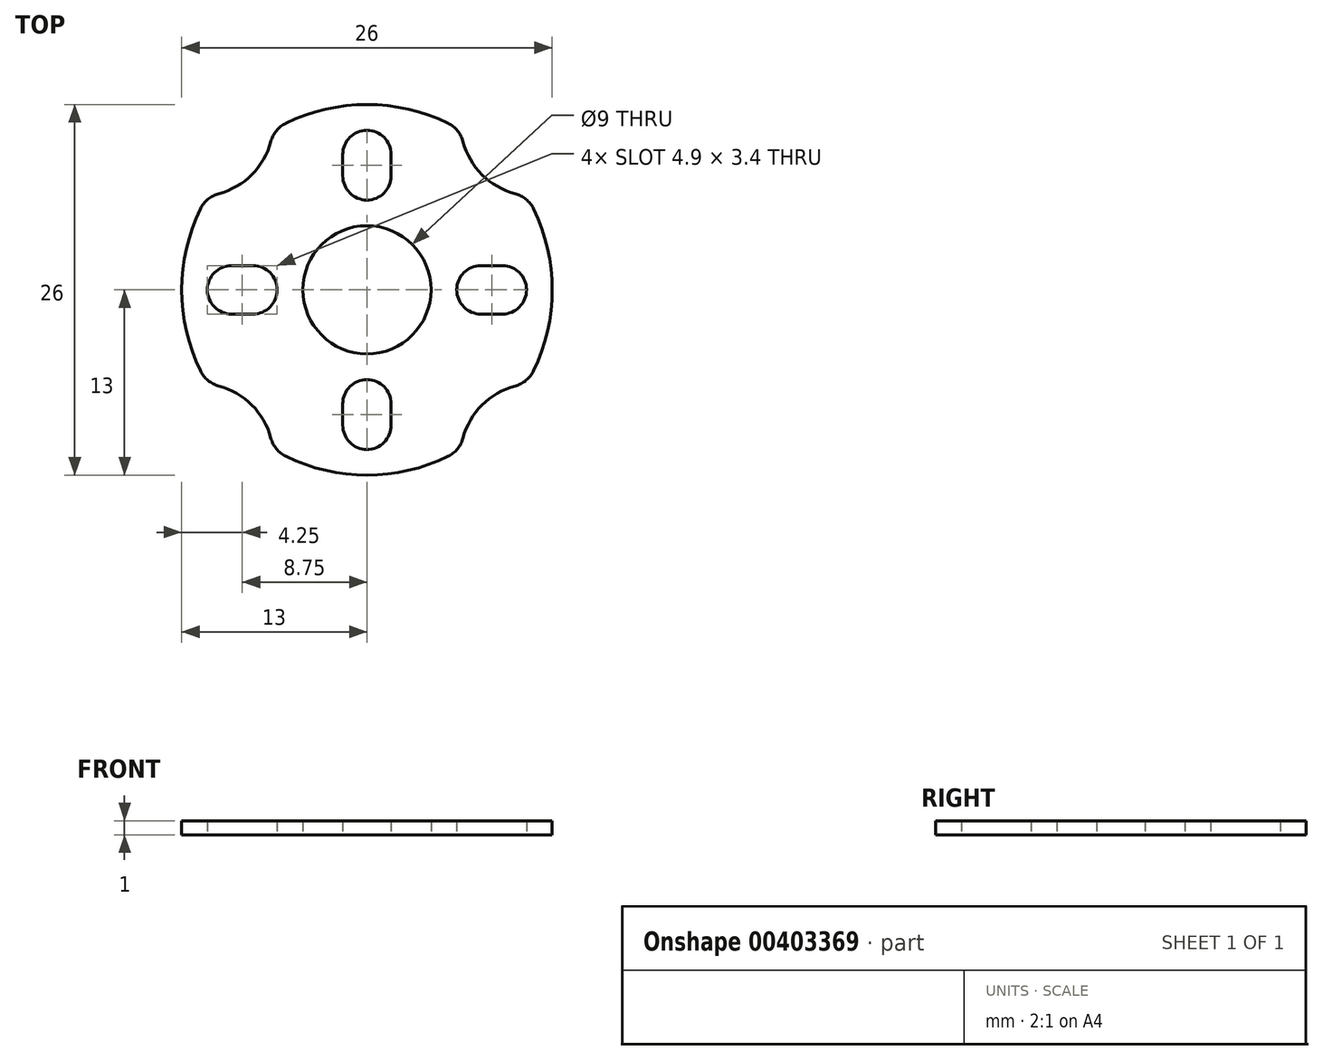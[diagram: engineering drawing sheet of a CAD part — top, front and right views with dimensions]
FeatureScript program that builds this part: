
annotation { "Feature Type Name" : "Feature", "Feature Type Description" : "" }
export const myFeature = defineFeature(function(context is Context, id is Id, definition is map)
    precondition{}
    {
        {
            assignVariable(context, id + "F0", {"name" : "padThickness", "anyValue" : 1});
        }
        {
            var Q0;
            Q0=qCreatedBy(makeId("Top.planeOp"),FACE);
            var sketch = newSketch(context, id + "F1", { "sketchPlane" : qUnion([Q0])});
            skLineSegment(sketch, "E0", {"start": v(-16.5, -1.7) * mm, "end": v(-16.5, -1.7) * mm});
            skLineSegment(sketch, "E1", {"start": v(-16.5, 1.7) * mm, "end": v(-8, 1.7) * mm});
            skLineSegment(sketch, "E2", {"start": v(1.7, 16.5) * mm, "end": v(1.7, 8) * mm});
            skLineSegment(sketch, "E3", {"start": v(-1.7, 16.5) * mm, "end": v(-1.7, 8) * mm});
            skLineSegment(sketch, "E4.MirrorCS", {"start": v(-1.7, -16.5) * mm, "end": v(-1.7, -16.5) * mm});
            skLineSegment(sketch, "E5.MirrorCS", {"start": v(1.7, -16.5) * mm, "end": v(1.7, -8) * mm});
            skLineSegment(sketch, "E6.MirrorCS", {"start": v(16.5, 1.7) * mm, "end": v(8, 1.7) * mm});
            skLineSegment(sketch, "E7.MirrorCS", {"start": v(16.5, -1.7) * mm, "end": v(8, -1.7) * mm});
            skArc(sketch, "E8", {"start": v(-1.7, 16.5) * mm, "mid": v(0, 14.8) * mm, "end": v(1.7, 16.5) * mm});
            skArc(sketch, "E9", {"start": v(1.7, 16.5) * mm, "mid": v(0, 18.2) * mm, "end": v(-1.7, 16.5) * mm});
            skLineSegment(sketch, "E10", {"start": v(-1.7, 8) * mm, "end": v(-1.7, 8) * mm});
            skLineSegment(sketch, "E11", {"start": v(8, 1.7) * mm, "end": v(8, 1.7) * mm});
            skArc(sketch, "E12", {"start": v(8, -1.7) * mm, "mid": v(6.3, 0) * mm, "end": v(8, 1.7) * mm});
            skArc(sketch, "E13", {"start": v(8, 1.7) * mm, "mid": v(9.7, 0) * mm, "end": v(8, -1.7) * mm});
            skArc(sketch, "E14", {"start": v(16.5, 1.7) * mm, "mid": v(18.2, 0) * mm, "end": v(16.5, -1.7) * mm});
            skArc(sketch, "E15", {"start": v(16.5, -1.7) * mm, "mid": v(14.8, 0) * mm, "end": v(16.5, 1.7) * mm});
            skLineSegment(sketch, "E16", {"start": v(1.7, -8) * mm, "end": v(1.7, -8) * mm});
            skArc(sketch, "E17", {"start": v(-1.7, -8) * mm, "mid": v(0, -6.3) * mm, "end": v(1.7, -8) * mm});
            skArc(sketch, "E18", {"start": v(1.7, -8) * mm, "mid": v(0, -9.7) * mm, "end": v(-1.7, -8) * mm});
            skLineSegment(sketch, "E19", {"start": v(-1.7, -16.5) * mm, "end": v(-1.7, -8) * mm});
            skArc(sketch, "E20", {"start": v(1.7, -16.5) * mm, "mid": v(0, -18.2) * mm, "end": v(-1.7, -16.5) * mm});
            skArc(sketch, "E21", {"start": v(-1.7, -16.5) * mm, "mid": v(0, -14.8) * mm, "end": v(1.7, -16.5) * mm});
            skLineSegment(sketch, "E22", {"start": v(-16.5, -1.7) * mm, "end": v(-8, -1.7) * mm});
            skArc(sketch, "E23", {"start": v(-16.5, -1.7) * mm, "mid": v(-14.8, 0) * mm, "end": v(-16.5, 1.7) * mm});
            skArc(sketch, "E24", {"start": v(-16.5, 1.7) * mm, "mid": v(-18.2, 0) * mm, "end": v(-16.5, -1.7) * mm});
            skArc(sketch, "E25", {"start": v(-8, 1.7) * mm, "mid": v(-9.7, 0) * mm, "end": v(-8, -1.7) * mm});
            skArc(sketch, "E26", {"start": v(-8, -1.7) * mm, "mid": v(-6.3, 0) * mm, "end": v(-8, 1.7) * mm});
            skArc(sketch, "E27", {"start": v(1.7, 8) * mm, "mid": v(0, 9.7) * mm, "end": v(-1.7, 8) * mm});
            skArc(sketch, "E28", {"start": v(-1.7, 8) * mm, "mid": v(0, 6.3) * mm, "end": v(1.7, 8) * mm});
            skArc(sketch, "E29.0", {"start": v(-16.5, 3.14) * mm, "mid": v(-18.72, 2.22) * mm, "end": v(-19.64, 0) * mm});
            skArc(sketch, "E30.0", {"start": v(0, 19.64) * mm, "mid": v(-2.22, 18.72) * mm, "end": v(-3.14, 16.5) * mm});
            skArc(sketch, "E31", {"start": v(-8, 3.14) * mm, "mid": v(-4.6, 4.6) * mm, "end": v(-3.14, 8) * mm});
            skLineSegment(sketch, "E32", {"start": v(-8, 3.14) * mm, "end": v(-16.5, 3.14) * mm});
            skLineSegment(sketch, "E33", {"start": v(-3.14, 8) * mm, "end": v(-3.14, 16.5) * mm});
            skPoint(sketch, "E34", {"position": v(-19.64, 0) * mm});
            skPoint(sketch, "E35", {"position": v(0, 19.64) * mm});
            skPoint(sketch, "E36", {"position": v(-4.6, 4.6) * mm});
            skArc(sketch, "E37.MirrorCS", {"start": v(0, 19.64) * mm, "mid": v(2.22, 18.72) * mm, "end": v(3.14, 16.5) * mm});
            skLineSegment(sketch, "E38.MirrorCS", {"start": v(8, 3.14) * mm, "end": v(16.5, 3.14) * mm});
            skLineSegment(sketch, "E39.MirrorCS", {"start": v(3.14, 8) * mm, "end": v(3.14, 16.5) * mm});
            skArc(sketch, "E40.MirrorCS", {"start": v(8, 3.14) * mm, "mid": v(4.6, 4.6) * mm, "end": v(3.14, 8) * mm});
            skArc(sketch, "E41.MirrorCS", {"start": v(16.5, 3.14) * mm, "mid": v(18.72, 2.22) * mm, "end": v(19.64, 0) * mm});
            skArc(sketch, "E42.MirrorCS", {"start": v(-16.5, -3.14) * mm, "mid": v(-18.72, -2.22) * mm, "end": v(-19.64, 0) * mm});
            skLineSegment(sketch, "E43.MirrorCS", {"start": v(-8, -3.14) * mm, "end": v(-16.5, -3.14) * mm});
            skArc(sketch, "E44.MirrorCS", {"start": v(-8, -3.14) * mm, "mid": v(-4.6, -4.6) * mm, "end": v(-3.14, -8) * mm});
            skLineSegment(sketch, "E45.MirrorCS", {"start": v(-3.14, -8) * mm, "end": v(-3.14, -16.5) * mm});
            skArc(sketch, "E46.MirrorCS", {"start": v(0, -19.64) * mm, "mid": v(-2.22, -18.72) * mm, "end": v(-3.14, -16.5) * mm});
            skArc(sketch, "E47.MirrorCS", {"start": v(0, -19.64) * mm, "mid": v(2.22, -18.72) * mm, "end": v(3.14, -16.5) * mm});
            skLineSegment(sketch, "E48.MirrorCS", {"start": v(8, -3.14) * mm, "end": v(16.5, -3.14) * mm});
            skLineSegment(sketch, "E49.MirrorCS", {"start": v(3.14, -8) * mm, "end": v(3.14, -16.5) * mm});
            skArc(sketch, "E50.MirrorCS", {"start": v(8, -3.14) * mm, "mid": v(4.6, -4.6) * mm, "end": v(3.14, -8) * mm});
            skArc(sketch, "E51.MirrorCS", {"start": v(16.5, -3.14) * mm, "mid": v(18.72, -2.22) * mm, "end": v(19.64, 0) * mm});
            skCircle(sketch, "E52", {"center": v(0, 0) * mm, "radius": 5.07 * mm});
            skSolve(sketch);
        }
        {
            var Q0;
            Q0=qCreatedBy(makeId("Top.planeOp"),FACE);
            var sketch = newSketch(context, id + "F2", { "sketchPlane" : qUnion([Q0])});
            skLineSegment(sketch, "E53", {"start": v(0, 0) * mm, "end": v(0, -13) * mm, "construction": true});
            skLineSegment(sketch, "E54", {"start": v(0, 0) * mm, "end": v(0, 13) * mm, "construction": true});
            skLineSegment(sketch, "E55", {"start": v(0, 0) * mm, "end": v(-13, 0) * mm, "construction": true});
            skLineSegment(sketch, "E56", {"start": v(0, 0) * mm, "end": v(13, 0) * mm, "construction": true});
            skCircle(sketch, "E57", {"center": v(0, 0) * mm, "radius": 13 * mm});
            skCircle(sketch, "E58", {"center": v(-9.5, 0) * mm, "radius": 1.7 * mm});
            skCircle(sketch, "E59", {"center": v(-8, 0) * mm, "radius": 1.7 * mm});
            skCircle(sketch, "E60.MirrorC", {"center": v(8, 0) * mm, "radius": 1.7 * mm});
            skCircle(sketch, "E61.MirrorC", {"center": v(9.5, 0) * mm, "radius": 1.7 * mm});
            skCircle(sketch, "E62", {"center": v(0, -8) * mm, "radius": 1.7 * mm});
            skCircle(sketch, "E63", {"center": v(0, -9.5) * mm, "radius": 1.7 * mm});
            skCircle(sketch, "E64.MirrorC", {"center": v(0, 9.5) * mm, "radius": 1.7 * mm});
            skCircle(sketch, "E65.MirrorC", {"center": v(0, 8) * mm, "radius": 1.7 * mm});
            skCircle(sketch, "E66", {"center": v(0, 0) * mm, "radius": 4.5 * mm});
            skLineSegment(sketch, "E67", {"start": v(14.85, -1.7) * mm, "end": v(-21.3, -1.7) * mm, "construction": true});
            skLineSegment(sketch, "E68", {"start": v(15.18, 1.7) * mm, "end": v(-24.63, 1.7) * mm, "construction": true});
            skLineSegment(sketch, "E69", {"start": v(-1.7, 14.2) * mm, "end": v(-1.7, -16.2) * mm, "construction": true});
            skLineSegment(sketch, "E70", {"start": v(1.7, 14.27) * mm, "end": v(1.7, -16.29) * mm, "construction": true});
            skLineSegment(sketch, "E71", {"start": v(-1.7, 9.5) * mm, "end": v(-1.7, 8) * mm});
            skLineSegment(sketch, "E72", {"start": v(1.7, 9.5) * mm, "end": v(1.7, 8) * mm});
            skLineSegment(sketch, "E73", {"start": v(-9.5, 1.7) * mm, "end": v(-8, 1.7) * mm});
            skLineSegment(sketch, "E74", {"start": v(-9.5, -1.7) * mm, "end": v(-8, -1.7) * mm});
            skLineSegment(sketch, "E75", {"start": v(9.5, 1.7) * mm, "end": v(8, 1.7) * mm});
            skLineSegment(sketch, "E76", {"start": v(8, -1.7) * mm, "end": v(9.5, -1.7) * mm});
            skLineSegment(sketch, "E77", {"start": v(-1.7, -8) * mm, "end": v(-1.7, -9.5) * mm});
            skLineSegment(sketch, "E78", {"start": v(1.7, -8) * mm, "end": v(1.7, -9.5) * mm});
            skLineSegment(sketch, "E79", {"start": v(0, 11.2) * mm, "end": v(-20.67, 11.2) * mm, "construction": true});
            skLineSegment(sketch, "E80", {"start": v(0, -11.2) * mm, "end": v(-20.67, -11.2) * mm, "construction": true});
            skLineSegment(sketch, "E81.MirrorCS", {"start": v(0, 11.2) * mm, "end": v(20.67, 11.2) * mm, "construction": true});
            skLineSegment(sketch, "E82.MirrorCS", {"start": v(0, -11.2) * mm, "end": v(20.67, -11.2) * mm, "construction": true});
            skLineSegment(sketch, "E83", {"start": v(-11.2, 0) * mm, "end": v(-11.2, 13.87) * mm, "construction": true});
            skLineSegment(sketch, "E84", {"start": v(-11.2, 0) * mm, "end": v(-11.2, -13.87) * mm, "construction": true});
            skLineSegment(sketch, "E85.MirrorCS", {"start": v(11.2, 0) * mm, "end": v(11.2, 13.87) * mm, "construction": true});
            skLineSegment(sketch, "E86.MirrorCS", {"start": v(11.2, 0) * mm, "end": v(11.2, -13.87) * mm, "construction": true});
            skArc(sketch, "E87", {"start": v(11.2, -6.6) * mm, "mid": v(8.08, -8.08) * mm, "end": v(6.6, -11.2) * mm});
            skArc(sketch, "E88.MirrorCS", {"start": v(11.2, 6.6) * mm, "mid": v(8.08, 8.08) * mm, "end": v(6.6, 11.2) * mm});
            skArc(sketch, "E89.MirrorCS", {"start": v(-11.2, -6.6) * mm, "mid": v(-8.08, -8.08) * mm, "end": v(-6.6, -11.2) * mm});
            skArc(sketch, "E90.MirrorCS", {"start": v(-11.2, 6.6) * mm, "mid": v(-8.08, 8.08) * mm, "end": v(-6.6, 11.2) * mm});
            skSolve(sketch);
        }
        {
            var Q0;
            Q0=makeQuery(id+"F2.imprint","IMPRINT",FACE,{"disambiguationData":[TD([[makeQuery(id+"F2.imprint","IMPRINT",EDGE,{"derivedFrom":sQuery(id+"F2.wireOp",EDGE,"E57")}),1.0]])]});
            extrude(context, id + "F3", {"entities" : qUnion([Q0]), "offsetDistance" : 25 * mm, "depth" : (getVariable(context, 'padThickness')) * mm});
        }
        {
            var Q0;
            {var subQ0=sQuery(id+"F2.wireOp",EDGE,"E89.MirrorCS");var subQ1=sQuery(id+"F2.wireOp",EDGE,"E57");Q0=makeQuery(id+"F3.opExtrude","SWEPT_EDGE",EDGE,{"disambiguationData":[OSD([subQ1,subQ0]),TDD([makeQuery(id+"F2.imprint","INTERSECT",VERTEX,{"disambiguationData":[OD(0.0)],"derivedFrom":[subQ1,subQ0]})])]});}
            var Q1;
            {var subQ0=sQuery(id+"F2.wireOp",EDGE,"E89.MirrorCS");var subQ1=sQuery(id+"F2.wireOp",EDGE,"E57");Q1=makeQuery(id+"F3.opExtrude","SWEPT_EDGE",EDGE,{"disambiguationData":[OSD([subQ1,subQ0]),TDD([makeQuery(id+"F2.imprint","INTERSECT",VERTEX,{"disambiguationData":[OD(1.0)],"derivedFrom":[subQ1,subQ0]})])]});}
            var Q2;
            {var subQ0=sQuery(id+"F2.wireOp",EDGE,"E87");var subQ1=sQuery(id+"F2.wireOp",EDGE,"E57");Q2=makeQuery(id+"F3.opExtrude","SWEPT_EDGE",EDGE,{"disambiguationData":[OSD([subQ1,subQ0]),TDD([makeQuery(id+"F2.imprint","INTERSECT",VERTEX,{"disambiguationData":[OD(1.0)],"derivedFrom":[subQ1,subQ0]})])]});}
            var Q3;
            {var subQ0=sQuery(id+"F2.wireOp",EDGE,"E87");var subQ1=sQuery(id+"F2.wireOp",EDGE,"E57");Q3=makeQuery(id+"F3.opExtrude","SWEPT_EDGE",EDGE,{"disambiguationData":[OSD([subQ1,subQ0]),TDD([makeQuery(id+"F2.imprint","INTERSECT",VERTEX,{"disambiguationData":[OD(0.0)],"derivedFrom":[subQ1,subQ0]})])]});}
            var Q4;
            {var subQ0=sQuery(id+"F2.wireOp",EDGE,"E88.MirrorCS");var subQ1=sQuery(id+"F2.wireOp",EDGE,"E57");Q4=makeQuery(id+"F3.opExtrude","SWEPT_EDGE",EDGE,{"disambiguationData":[OSD([subQ1,subQ0]),TDD([makeQuery(id+"F2.imprint","INTERSECT",VERTEX,{"disambiguationData":[OD(0.0)],"derivedFrom":[subQ1,subQ0]})])]});}
            var Q5;
            {var subQ0=sQuery(id+"F2.wireOp",EDGE,"E88.MirrorCS");var subQ1=sQuery(id+"F2.wireOp",EDGE,"E57");Q5=makeQuery(id+"F3.opExtrude","SWEPT_EDGE",EDGE,{"disambiguationData":[OSD([subQ1,subQ0]),TDD([makeQuery(id+"F2.imprint","INTERSECT",VERTEX,{"disambiguationData":[OD(1.0)],"derivedFrom":[subQ1,subQ0]})])]});}
            var Q6;
            {var subQ0=sQuery(id+"F2.wireOp",EDGE,"E90.MirrorCS");var subQ1=sQuery(id+"F2.wireOp",EDGE,"E57");Q6=makeQuery(id+"F3.opExtrude","SWEPT_EDGE",EDGE,{"disambiguationData":[OSD([subQ1,subQ0]),TDD([makeQuery(id+"F2.imprint","INTERSECT",VERTEX,{"disambiguationData":[OD(1.0)],"derivedFrom":[subQ1,subQ0]})])]});}
            var Q7;
            {var subQ0=sQuery(id+"F2.wireOp",EDGE,"E90.MirrorCS");var subQ1=sQuery(id+"F2.wireOp",EDGE,"E57");Q7=makeQuery(id+"F3.opExtrude","SWEPT_EDGE",EDGE,{"disambiguationData":[OSD([subQ1,subQ0]),TDD([makeQuery(id+"F2.imprint","INTERSECT",VERTEX,{"disambiguationData":[OD(0.0)],"derivedFrom":[subQ1,subQ0]})])]});}
            fillet(context, id + "F4", {"entities" : qUnion([Q0, Q1, Q2, Q3, Q4, Q5, Q6, Q7]), "radius" : 2 * mm, "tangentPropagation" : true, "allowEdgeOverflow" : false});
        }
    });
